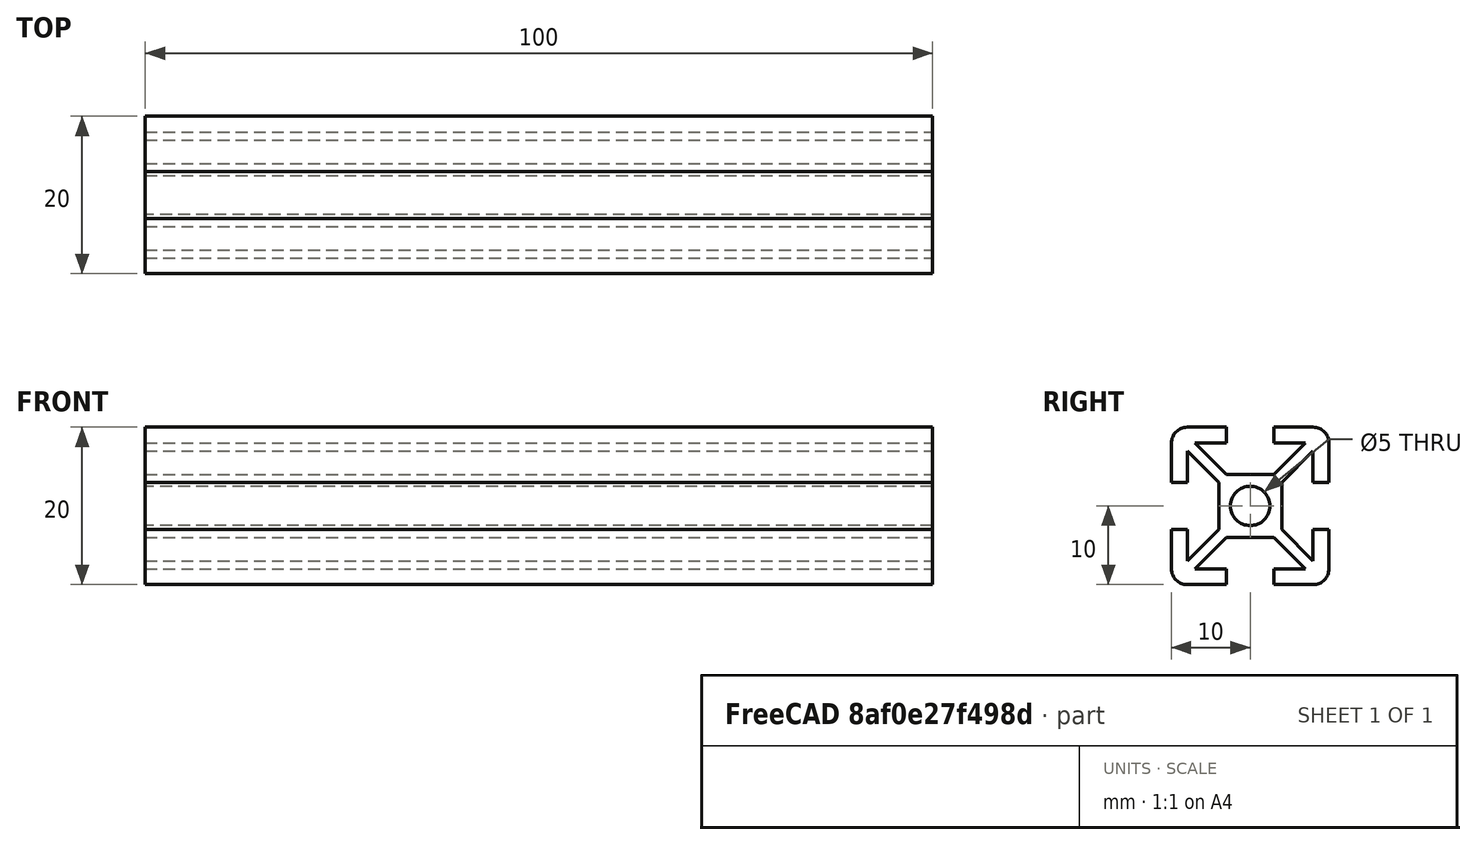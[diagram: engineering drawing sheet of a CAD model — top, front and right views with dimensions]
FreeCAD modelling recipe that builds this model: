
FCSTD DOCUMENT  (FreeCAD 0.19R24267 +99 (Git))
Label: 2020 Rail strut panel carrier near feet 100mm
License: All rights reserved
LicenseURL: http://en.wikipedia.org/wiki/All_rights_reserved
objects: Sketcher::SketchObject×1, PartDesign::Pad×1, PartDesign::Body×1
note: 4 computed .brp shape members not serialized (recipe doc carries the construction recipe); baked Part::Feature solids carry a one-line shape summary decoded from their .brp

FEATURE [Sketcher::SketchObject] Sketch  label="Rail cross section"
  FullyConstrained = true
  MapMode = 5
  Placement = pos=(0,0,0) rot=(0.57735,0.57735,0.57735;2.0944rad)
  Support = -> [YZ_Plane]
  sketch-geometry (47):
    g0: ArcOfCircle CenterX=-8 CenterY=8 CenterZ=0 NormalX=0 NormalY=0 NormalZ=1 AngleXU=0 Radius=2 StartAngle=1.5708 EndAngle=3.14159
    g1: ArcOfCircle CenterX=-8 CenterY=-8 CenterZ=0 NormalX=0 NormalY=0 NormalZ=1 AngleXU=0 Radius=2 StartAngle=3.14159 EndAngle=4.71239
    g2: ArcOfCircle CenterX=8 CenterY=-8 CenterZ=0 NormalX=0 NormalY=0 NormalZ=1 AngleXU=0 Radius=2 StartAngle=4.71239 EndAngle=6.28319
    g3: ArcOfCircle CenterX=8 CenterY=8 CenterZ=0 NormalX=0 NormalY=0 NormalZ=1 AngleXU=0 Radius=2 StartAngle=1e-16 EndAngle=1.5708
    g4: Circle CenterX=0 CenterY=0 CenterZ=0 NormalX=0 NormalY=0 NormalZ=1 AngleXU=0 Radius=2.5
    g5: LineSegment StartX=-10 StartY=8 StartZ=0 EndX=-10 EndY=3 EndZ=0
    g6: LineSegment StartX=-10 StartY=-3 StartZ=0 EndX=-10 EndY=-8 EndZ=0
    g7: LineSegment StartX=-8 StartY=-10 StartZ=0 EndX=-3 EndY=-10 EndZ=0
    g8: LineSegment StartX=3 StartY=-10 StartZ=0 EndX=8 EndY=-10 EndZ=0
    g9: LineSegment StartX=10 StartY=-8 StartZ=0 EndX=10 EndY=-3 EndZ=0
    g10: LineSegment StartX=10 StartY=3 StartZ=0 EndX=10 EndY=8 EndZ=0
    g11: LineSegment StartX=-8 StartY=10 StartZ=0 EndX=-3 EndY=10 EndZ=0
    g12: LineSegment StartX=3 StartY=10 StartZ=0 EndX=8 EndY=10 EndZ=0
    g13: LineSegment StartX=-3 StartY=4 StartZ=0 EndX=3 EndY=4 EndZ=0
    g14: LineSegment StartX=4 StartY=3 StartZ=0 EndX=4 EndY=-3 EndZ=0
    g15: LineSegment StartX=3 StartY=-4 StartZ=0 EndX=-3 EndY=-4 EndZ=0
    g16: LineSegment StartX=-4 StartY=-3 StartZ=0 EndX=-4 EndY=3 EndZ=0
    g17: LineSegment StartX=-3 StartY=-4 StartZ=0 EndX=-7 EndY=-8 EndZ=0
    g18: LineSegment StartX=-3 StartY=-10 StartZ=0 EndX=-3 EndY=-8 EndZ=0
    g19: LineSegment StartX=3 StartY=-4 StartZ=0 EndX=7 EndY=-8 EndZ=0
    g20: LineSegment StartX=4 StartY=-3 StartZ=0 EndX=8 EndY=-7 EndZ=0
    g21: LineSegment StartX=8 StartY=-7 StartZ=0 EndX=8 EndY=-3 EndZ=0
    g22: LineSegment StartX=10 StartY=-3 StartZ=0 EndX=8 EndY=-3 EndZ=0
    g23: LineSegment StartX=4 StartY=3 StartZ=0 EndX=8 EndY=7 EndZ=0
    g24: LineSegment StartX=8 StartY=7 StartZ=0 EndX=8 EndY=3 EndZ=0
    g25: LineSegment StartX=8 StartY=3 StartZ=0 EndX=10 EndY=3 EndZ=0
    g26: LineSegment StartX=3 StartY=10 StartZ=0 EndX=3 EndY=8 EndZ=0
    g27: LineSegment StartX=3 StartY=8 StartZ=0 EndX=7 EndY=8 EndZ=0
    g28: LineSegment StartX=7 StartY=8 StartZ=0 EndX=3 EndY=4 EndZ=0
    g29: LineSegment StartX=-3 StartY=4 StartZ=0 EndX=-7 EndY=8 EndZ=0
    g30: LineSegment StartX=-7 StartY=8 StartZ=0 EndX=-3 EndY=8 EndZ=0
    g31: LineSegment StartX=-3 StartY=8 StartZ=0 EndX=-3 EndY=10 EndZ=0
    g32: LineSegment StartX=-4 StartY=3 StartZ=0 EndX=-8 EndY=7 EndZ=0
    g33: LineSegment StartX=-8 StartY=3 StartZ=0 EndX=-10 EndY=3 EndZ=0
    g34: LineSegment StartX=-10 StartY=-3 StartZ=0 EndX=-8 EndY=-3 EndZ=0
    g35: LineSegment StartX=-8 StartY=-7 StartZ=0 EndX=-4 EndY=-3 EndZ=0
    g36: LineSegment StartX=3 StartY=-10 StartZ=0 EndX=3 EndY=-8 EndZ=0
    g37: LineSegment StartX=3 StartY=-8 StartZ=0 EndX=7 EndY=-8 EndZ=0
    g38: LineSegment StartX=-3 StartY=-8 StartZ=0 EndX=-7 EndY=-8 EndZ=0
    g39: LineSegment StartX=-8 StartY=-7 StartZ=0 EndX=-8 EndY=-3 EndZ=0
    g40: LineSegment StartX=-8 StartY=3 StartZ=0 EndX=-8 EndY=7 EndZ=0
    g41: LineSegment StartX=-3 StartY=10 StartZ=0 EndX=3 EndY=10 EndZ=0
    g42: LineSegment StartX=10 StartY=3 StartZ=0 EndX=10 EndY=-3 EndZ=0
    g43: LineSegment StartX=3 StartY=-10 StartZ=0 EndX=-3 EndY=-10 EndZ=0
    g44: LineSegment StartX=-10 StartY=-3 StartZ=0 EndX=-10 EndY=3 EndZ=0
    g45: LineSegment StartX=-4 StartY=-3 StartZ=0 EndX=-3 EndY=-4 EndZ=0
    g46: LineSegment StartX=-8 StartY=-7 StartZ=0 EndX=-7 EndY=-8 EndZ=0
  constraints (128):
    c: Radius(g0) = 2  'ASSUMED EDGE RADIUS'
    c: Equal(g1,g2)
    c: Coincident(g4,g-1)
    c: Radius(g4) = 2.5  'CENTER HOLE'
    c: Vertical(g6)
    c: Horizontal(g7)
    c: Horizontal(g8)
    c: Vertical(g9)
    c: Vertical(g10)
    c: Horizontal(g11)
    c: Horizontal(g12)
    c: DistanceX(g0,g3) = 20  'RAIL WIDTH'
    c: Vertical(g5)
    c: DistanceY(g2,g3) = 20  'RAIL HEIGHT'
    c: DistanceX(g7,g8) = 6  'SLOT WIDTH'
    c: Equal(g8,g7)
    c: Equal(g7,g6)
    c: Equal(g5,g11)
    c: Equal(g12,g10)
    c: Tangent(g12,g3) = 1.5708
    c: Tangent(g10,g3) = -1.5708
    c: Tangent(g11,g0) = 1.5708
    c: Tangent(g5,g0) = -1.5708
    c: Tangent(g6,g1) = -1.5708
    c: Tangent(g7,g1) = -1.5708
    c: Tangent(g8,g2) = -1.5708
    c: Tangent(g9,g2) = -1.5708
    c: Symmetric(g3,g2,g-1)
    c: Symmetric(g0,g3,g-2)
    c: Horizontal(g13)
    c: Vertical(g14)
    c: Vertical(g16)
    c: Horizontal(g15)
    c: Equal(g16,g15)
    c: Equal(g15,g14)
    c: Coincident(g17,g15)
    c: Coincident(g18,g7)
    c: Vertical(g18)
    c: Coincident(g19,g15)
    c: Coincident(g20,g14)
    c: Coincident(g21,g20)
    c: Vertical(g21)
    c: Coincident(g22,g9)
    c: Coincident(g22,g21)
    c: Coincident(g23,g14)
    c: Coincident(g24,g23)
    c: Vertical(g24)
    c: Coincident(g25,g24)
    c: Coincident(g25,g10)
    c: Coincident(g26,g12)
    c: Vertical(g26)
    c: Coincident(g27,g26)
    c: Horizontal(g27)
    c: Coincident(g28,g27)
    c: Coincident(g28,g13)
    c: Coincident(g29,g13)
    c: Coincident(g30,g29)
    c: Horizontal(g30)
    c: Coincident(g31,g30)
    c: Coincident(g31,g11)
    c: Coincident(g32,g16)
    c: Coincident(g33,g5)
    c: Horizontal(g33)
    c: Coincident(g34,g6)
    c: Horizontal(g34)
    c: Coincident(g35,g16)
    c: Coincident(g36,g8)
    c: Vertical(g36)
    c: Coincident(g37,g36)
    c: Coincident(g37,g19)
    c: Coincident(g38,g18)
    c: Coincident(g38,g17)
    c: Horizontal(g38)
    c: Coincident(g39,g35)
    c: Coincident(g39,g34)
    c: Vertical(g39)
    c: Coincident(g40,g33)
    c: Coincident(g40,g32)
    c: Vertical(g40)
    c: Horizontal(g37)
    c: Horizontal(g25)
    c: Horizontal(g22)
    c: Equal(g38,g37)
    c: Equal(g37,g21)
    c: Equal(g21,g24)
    c: Equal(g24,g27)
    c: Equal(g27,g30)
    c: Equal(g30,g40)
    c: Equal(g40,g39)
    c: Vertical(g31)
    c: Equal(g31,g26)
    c: Equal(g26,g25)
    c: Equal(g25,g22)
    c: Equal(g22,g36)
    c: Equal(g36,g18)
    c: Equal(g18,g34)
    c: Equal(g34,g33)
    c: Equal(g32,g29)
    c: Equal(g29,g28)
    c: Equal(g28,g23)
    c: Equal(g23,g20)
    c: Equal(g20,g19)
    c: Equal(g19,g17)
    c: Equal(g17,g35)
    c: Coincident(g41,g11)
    c: Coincident(g41,g12)
    c: Coincident(g42,g10)
    c: Coincident(g42,g9)
    c: Coincident(g43,g8)
    c: Coincident(g43,g7)
    c: Horizontal(g43)
    c: Coincident(g44,g6)
    c: Coincident(g44,g5)
    c: Vertical(g44)
    c: Horizontal(g41)
    c: DistanceY(g8,g15) = 6  'ASSUMED SLOT DEPTH'
    c: Equal(g43,g15)
    c: Equal(g16,g13)
    c: Equal(g44,g43)
    c: Equal(g43,g42)
    c: Equal(g42,g41)
    c: Vertical(g42)
    c: DistanceY(g36,g36) = 2  'ASSUMED WALL THICKNESS'
    c: Coincident(g45,g16)
    c: Coincident(g45,g15)
    c: Coincident(g46,g35)
    c: Coincident(g46,g17)
    c: Equal(g45,g46)
FEATURE [PartDesign::Pad] Pad  label="Length"
  Direction = (1,1,1)
  Length = 100
  Length2 = 100
  Placement = pos=(0,0,0) rot=(0.57735,0.57735,0.57735;2.0944rad)
  Profile = -> Sketch
  Type = 0
FEATURE [PartDesign::Body] Body
  Group = -> [Sketch,Pad]
  Origin = -> Origin
  Tip = -> Pad
